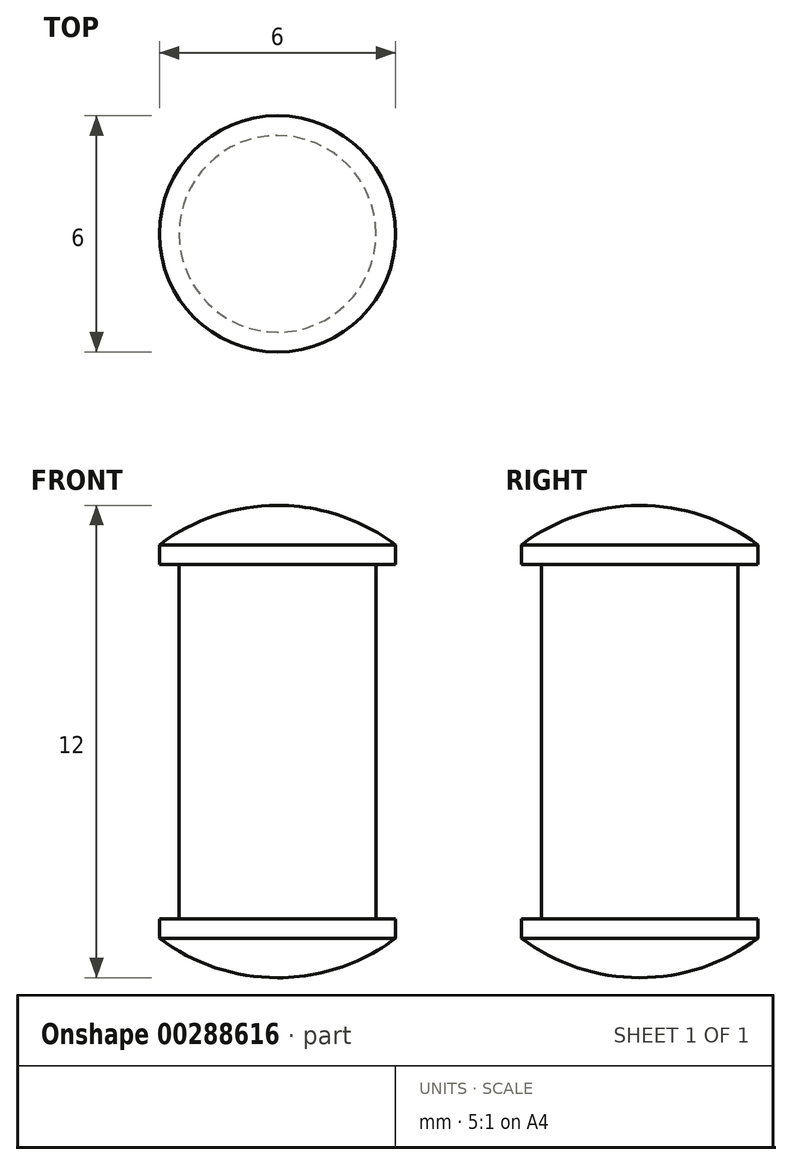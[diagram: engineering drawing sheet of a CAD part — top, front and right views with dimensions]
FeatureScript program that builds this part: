
annotation { "Feature Type Name" : "Feature", "Feature Type Description" : "" }
export const myFeature = defineFeature(function(context is Context, id is Id, definition is map)
    precondition{}
    {
        {
            var Q0;
            Q0=qCreatedBy(makeId("Front.planeOp"),FACE);
            var sketch = newSketch(context, id + "F0", { "sketchPlane" : qUnion([Q0])});
            skLineSegment(sketch, "E0", {"start": v(0, 0) * mm, "end": v(0, 5) * mm});
            skLineSegment(sketch, "E1", {"start": v(0, 5) * mm, "end": v(-3, 5) * mm});
            skLineSegment(sketch, "E2", {"start": v(-3, 5) * mm, "end": v(-3, 4.5) * mm});
            skLineSegment(sketch, "E3", {"start": v(-3, 4.5) * mm, "end": v(-2.5, 4.5) * mm});
            skLineSegment(sketch, "E4", {"start": v(-2.5, 4.5) * mm, "end": v(-2.5, 0) * mm});
            skLineSegment(sketch, "E5", {"start": v(-2.5, 0) * mm, "end": v(0, 0) * mm});
            skPoint(sketch, "E6", {"position": v(0, 6) * mm});
            skArc(sketch, "E7", {"start": v(0, 6) * mm, "mid": v(-1.58, 5.74) * mm, "end": v(-3, 5) * mm});
            skLineSegment(sketch, "E8", {"start": v(0, 6) * mm, "end": v(0, 5) * mm});
            skPoint(sketch, "E9.MirrorCS.end.orphan", {"position": v(3, 5) * mm});
            skPoint(sketch, "E9.MirrorCS.start.orphan", {"position": v(0, 5) * mm});
            skSolve(sketch);
        }
        {
            var Q0;
            Q0=makeQuery(id+"F0.imprint","IMPRINT",FACE,{"disambiguationData":[TD([[makeQuery(id+"F0.imprint","IMPRINT",EDGE,{"derivedFrom":sQuery(id+"F0.wireOp",EDGE,"E0")}),1.0]])]});
            var Q1;
            Q1=makeQuery(id+"F0.imprint","IMPRINT",FACE,{"disambiguationData":[TD([[makeQuery(id+"F0.imprint","IMPRINT",EDGE,{"derivedFrom":sQuery(id+"F0.wireOp",EDGE,"E1")}),-1.0]])]});
            var Q2;
            Q2=sQuery(id+"F0.wireOp",EDGE,"E0");
            revolve(context, id + "F1", {"entities" : qUnion([Q0, Q1]), "axis" : qUnion([Q2]), "revolveType" : RevolveType.FULL});
        }
        {
            var Q0;
            Q0=makeQuery(id+"F1.opRevolve","SWEPT_BODY",BODY,{"disambiguationData":[OSD([sQuery(id+"F0.wireOp",EDGE,"E0"),sQuery(id+"F0.wireOp",EDGE,"E2"),sQuery(id+"F0.wireOp",EDGE,"E3"),sQuery(id+"F0.wireOp",EDGE,"E4"),sQuery(id+"F0.wireOp",EDGE,"E5"),sQuery(id+"F0.wireOp",EDGE,"E7"),sQuery(id+"F0.wireOp",EDGE,"E8")])]});
            var Q1;
            Q1=makeQuery(id+"F1.opRevolve","SWEPT_FACE",FACE,{"disambiguationData":[OSD([sQuery(id+"F0.wireOp",EDGE,"E5")])]});
            mirror(context, id + "F2", {"operationType" : NewBodyOperationType.ADD, "entities" : qUnion([Q0]), "mirrorPlane" : qUnion([Q1])});
        }
    });
